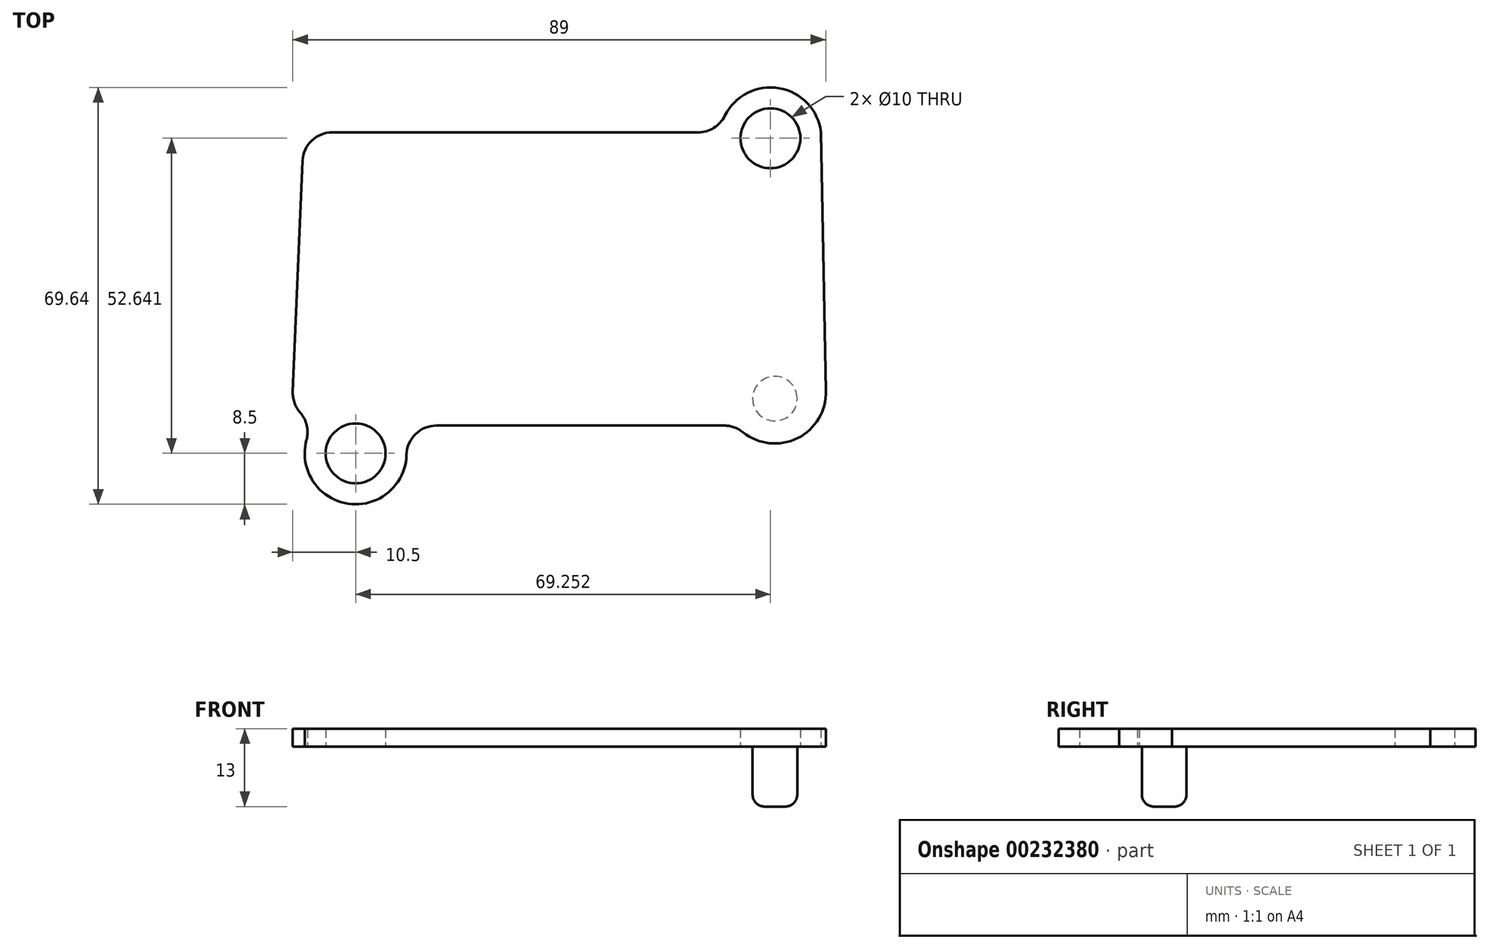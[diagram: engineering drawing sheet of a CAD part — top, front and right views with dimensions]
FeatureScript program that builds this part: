
annotation { "Feature Type Name" : "Feature", "Feature Type Description" : "" }
export const myFeature = defineFeature(function(context is Context, id is Id, definition is map)
    precondition{}
    {
        {
            var Q0;
            Q0=qCreatedBy(makeId("Top.planeOp"),FACE);
            var sketch = newSketch(context, id + "F0", { "sketchPlane" : qUnion([Q0])});
            skCircle(sketch, "E0", {"center": v(70, 10.15) * mm, "radius": 3.5 * mm, "construction": true});
            skArc(sketch, "E1", {"start": v(77.73, 52) * mm, "mid": v(71.5, 60.84) * mm, "end": v(61.64, 56.42) * mm});
            skArc(sketch, "E2", {"start": v(64.66, 3.54) * mm, "mid": v(73.81, 2.55) * mm, "end": v(78.5, 10.48) * mm});
            skLineSegment(sketch, "E3", {"start": v(61.51, 4.65) * mm, "end": v(13.5, 4.65) * mm});
            skLineSegment(sketch, "E4", {"start": v(-3.88, 53.64) * mm, "end": v(57.16, 53.64) * mm});
            skLineSegment(sketch, "E5", {"start": v(-9.26, 39.65) * mm, "end": v(-8.87, 48.85) * mm});
            skLineSegment(sketch, "E6", {"start": v(0, 0) * mm, "end": v(-5, 0) * mm, "construction": true});
            skLineSegment(sketch, "E7", {"start": v(77.7, 53.59) * mm, "end": v(78.5, 10.48) * mm});
            skPoint(sketch, "E8.visualSharp", {"position": v(-8.67, 53.64) * mm});
            skArc(sketch, "E8.filletArc", {"start": v(-3.88, 53.64) * mm, "mid": v(-7.34, 52.25) * mm, "end": v(-8.87, 48.85) * mm});
            skLineSegment(sketch, "E9", {"start": v(-9.26, 39.65) * mm, "end": v(-10.5, 10.33) * mm});
            skLineSegment(sketch, "E10.filletArc", {"start": v(-9.55, 4.21) * mm, "end": v(-9.55, 4.21) * mm});
            skPoint(sketch, "E11.visualSharp", {"position": v(63.52, 4.65) * mm});
            skArc(sketch, "E11.filletArc", {"start": v(64.66, 3.54) * mm, "mid": v(63.18, 4.36) * mm, "end": v(61.51, 4.65) * mm});
            skPoint(sketch, "E12.visualSharp", {"position": v(60.81, 53.64) * mm});
            skArc(sketch, "E12.filletArc", {"start": v(57.16, 53.64) * mm, "mid": v(59.8, 54.4) * mm, "end": v(61.64, 56.42) * mm});
            skPoint(sketch, "E13", {"position": v(70.34, 13.63) * mm});
            skCircle(sketch, "E14", {"center": v(69.25, 52.64) * mm, "radius": 5 * mm});
            skCircle(sketch, "E15", {"center": v(0, 0) * mm, "radius": 5 * mm});
            skLineSegment(sketch, "E16", {"start": v(70, 10.15) * mm, "end": v(70, -0.31) * mm, "construction": true});
            skArc(sketch, "E17", {"start": v(-8.2, 2.23) * mm, "mid": v(-1.23, -8.41) * mm, "end": v(8.5, -0.22) * mm});
            skLineSegment(sketch, "E18", {"start": v(-10.02, 7.53) * mm, "end": v(-10.6, 7.97) * mm});
            skPoint(sketch, "E19.visualSharp", {"position": v(7.12, 4.65) * mm});
            skArc(sketch, "E19.filletArc", {"start": v(13.5, 4.65) * mm, "mid": v(10, 3.23) * mm, "end": v(8.5, -0.22) * mm});
            skPoint(sketch, "E20.visualSharp", {"position": v(-6.8, 5.1) * mm});
            skArc(sketch, "E20.filletArc", {"start": v(-8.2, 2.23) * mm, "mid": v(-8.16, 4.66) * mm, "end": v(-9.26, 6.83) * mm});
            skArc(sketch, "E21.filletArc", {"start": v(-10.5, 10.33) * mm, "mid": v(-10.22, 8.46) * mm, "end": v(-9.26, 6.83) * mm});
            skSolve(sketch);
        }
        {
            var Q0;
            {var subQ4=sQuery(id+"F0.wireOp",EDGE,"E2");Q0=makeQuery(id+"F0.imprint","IMPRINT",FACE,{"disambiguationData":[TD([[makeQuery(id+"F0.imprint","IMPRINT",EDGE,{"derivedFrom":subQ4}),1.0]])]});}
            extrude(context, id + "F1", {"entities" : qUnion([Q0]), "depth" : 3 * mm});
        }
        {
            var Q0;
            Q0=makeQuery(id+"F1.opExtrude","CAP_FACE",FACE,{"disambiguationData":[OSD([sQuery(id+"F0.wireOp",EDGE,"6f26e20c-6914-44fa-ba04-4538a46e5daa"),sQuery(id+"F0.wireOp",EDGE,"041ff5fd-8a31-486e-9c75-8d0426b4d997"),sQuery(id+"F0.wireOp",EDGE,"E1"),sQuery(id+"F0.wireOp",EDGE,"E2"),sQuery(id+"F0.wireOp",EDGE,"f8d61b12-a4ac-4b25-87bf-e2bb1264f5c6"),sQuery(id+"F0.wireOp",EDGE,"E3"),sQuery(id+"F0.wireOp",EDGE,"E4"),sQuery(id+"F0.wireOp",EDGE,"E5"),sQuery(id+"F0.wireOp",EDGE,"E7"),sQuery(id+"F0.wireOp",EDGE,"E8.filletArc"),sQuery(id+"F0.wireOp",EDGE,"E9"),sQuery(id+"F0.wireOp",EDGE,"HrAu2aMs-rrN2-khm5-BbhH-4SxwlaALr5xd"),sQuery(id+"F0.wireOp",EDGE,"3GxJHeRS-0IFX-Vn1Y-7GA1-5yosB6Asuusd"),sQuery(id+"F0.wireOp",EDGE,"86fee0ae-c232-4c38-b7d0-e2189f2c94ab.filletArc"),sQuery(id+"F0.wireOp",EDGE,"b732ce32-6db5-4a36-bfc9-88095b56862b.filletArc"),sQuery(id+"F0.wireOp",EDGE,"4c49eee0-4f62-4b3d-a858-9c5cc85e5989.filletArc"),sQuery(id+"F0.wireOp",EDGE,"E11.filletArc"),sQuery(id+"F0.wireOp",EDGE,"E12.filletArc")])],"isStart":true});
            var sketch = newSketch(context, id + "F2", { "sketchPlane" : qUnion([Q0])});
            skCircle(sketch, "E22", {"center": v(70, -10.15) * mm, "radius": 8.5 * mm, "construction": true});
            skLineSegment(sketch, "E23", {"start": v(70, -10.15) * mm, "end": v(70, 2.79) * mm, "construction": true});
            skPoint(sketch, "E24", {"position": v(70, -9.15) * mm});
            skCircle(sketch, "E25", {"center": v(70, -9.15) * mm, "radius": 3.73 * mm});
            skSolve(sketch);
        }
        {
            var Q0;
            Q0=makeQuery(id+"F2.imprint","IMPRINT",FACE,{"disambiguationData":[TD([[makeQuery(id+"F2.imprint","IMPRINT",EDGE,{"derivedFrom":sQuery(id+"F2.wireOp",EDGE,"E25")}),1.0]])]});
            var Q1;
            Q1=sQuery(id+"F2.wireOp",EDGE,"c5c5bb78-30f6-4926-8b18-05c0ca30b007");
            extrude(context, id + "F3", {"entities" : qUnion([Q0]), "surfaceEntities" : qUnion([Q1]), "depth" : 10 * mm});
        }
        {
            var Q0;
            Q0=makeQuery(id+"F3.opExtrude","CAP_EDGE",EDGE,{"disambiguationData":[OSD([sQuery(id+"F2.wireOp",EDGE,"E25")])],"isStart":false});
            fillet(context, id + "F4", {"entities" : qUnion([Q0]), "radius" : 2 * mm, "tangentPropagation" : true, "allowEdgeOverflow" : false});
        }
    });
